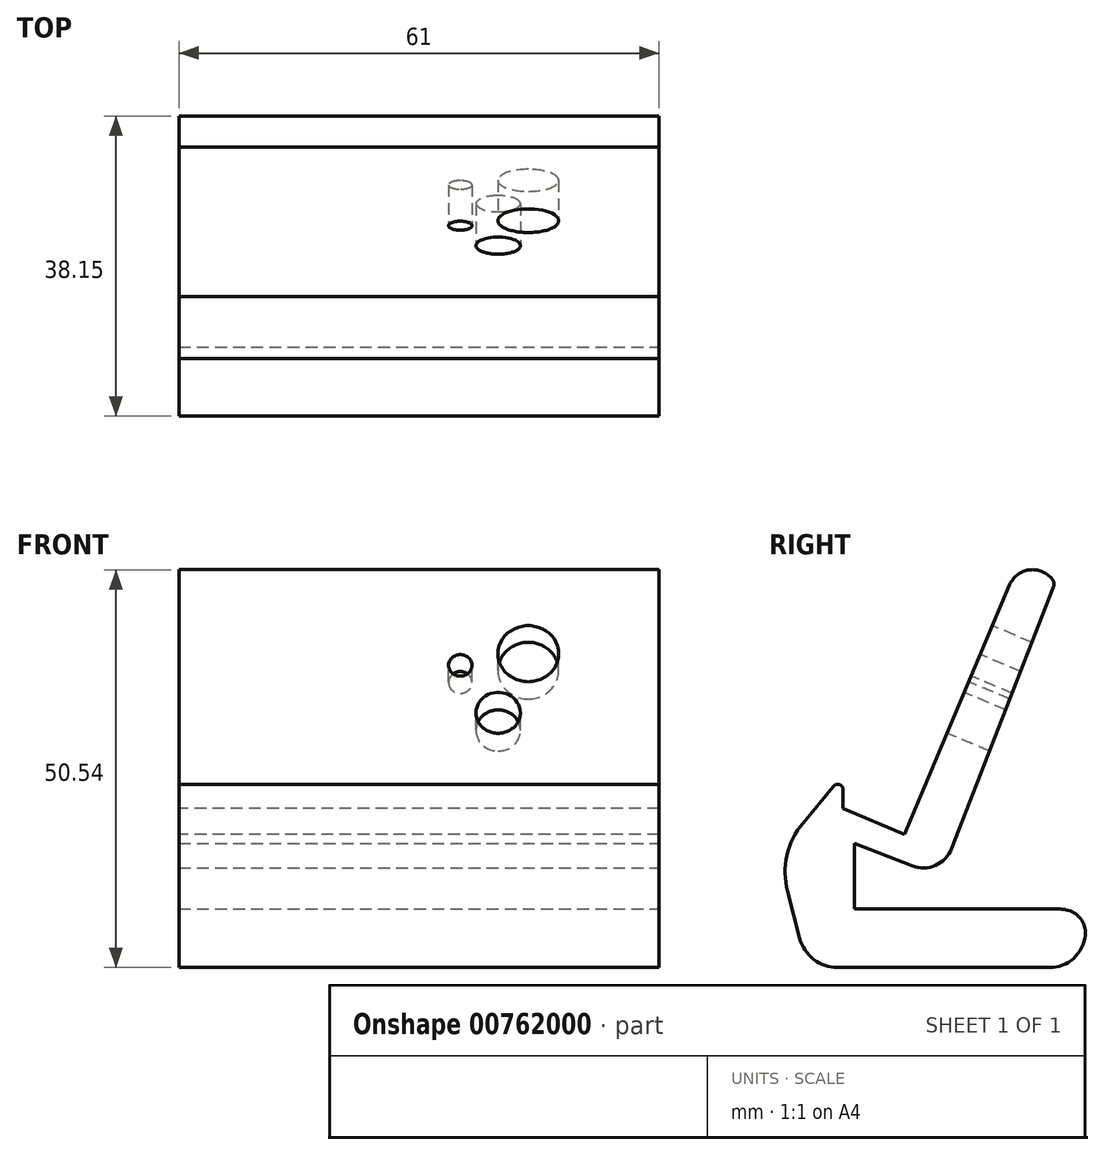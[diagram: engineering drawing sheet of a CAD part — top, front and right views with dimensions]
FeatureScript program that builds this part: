
annotation { "Feature Type Name" : "Feature", "Feature Type Description" : "" }
export const myFeature = defineFeature(function(context is Context, id is Id, definition is map)
    precondition{}
    {
        {
            var Q0;
            Q0=qCreatedBy(makeId("Right.planeOp"),FACE);
            var sketch = newSketch(context, id + "F0", { "sketchPlane" : qUnion([Q0])});
            skLineSegment(sketch, "E0", {"start": v(4.97, 18.95) * mm, "end": v(-10.62, -18.14) * mm});
            skLineSegment(sketch, "E1", {"start": v(-10.62, -18.14) * mm, "end": v(-18.45, -14.85) * mm});
            skLineSegment(sketch, "E2", {"start": v(-18.45, -14.85) * mm, "end": v(-18.45, -10.62) * mm});
            skLineSegment(sketch, "E3", {"start": v(-18.45, -10.62) * mm, "end": v(-26.74, -20.56) * mm});
            skLineSegment(sketch, "E4", {"start": v(-26.74, -20.56) * mm, "end": v(-22.98, -35.08) * mm});
            skLineSegment(sketch, "E5", {"start": v(-22.98, -35.08) * mm, "end": v(18.14, -35.08) * mm});
            skFitSpline(sketch, "E6", {"points": [v(18.14, -35.08) * mm, v(4.97, 18.95) * mm], "startDerivative": vector(-54.43, 31.45) * mm, "endDerivative": vector(-48.38, 56.85) * mm});
            skSolve(sketch);
        }
        {
            var Q0;
            Q0 = qSketchRegion(id + "F0", true);
            extrude(context, id + "F1", {"entities" : qUnion([Q0]), "depth" : 61 * mm, "offsetDistance" : 25 * mm});
        }
        {
            var Q0;
            Q0=makeQuery(id+"F1.opExtrude","SWEPT_EDGE",EDGE,{"disambiguationData":[OSD([sQuery(id+"F0.wireOp",EDGE,"E3"),sQuery(id+"F0.wireOp",EDGE,"E4")])]});
            fillet(context, id + "F2", {"entities" : qUnion([Q0]), "radius" : 9.67 * mm, "tangentPropagation" : true, "allowEdgeOverflow" : false});
        }
        {
            var Q0;
            Q0=makeQuery(id+"F1.opExtrude","SWEPT_EDGE",EDGE,{"disambiguationData":[OSD([sQuery(id+"F0.wireOp",EDGE,"E2"),sQuery(id+"F0.wireOp",EDGE,"E3")])]});
            fillet(context, id + "F3", {"entities" : qUnion([Q0]), "radius" : 0.67 * mm, "tangentPropagation" : true, "allowEdgeOverflow" : false});
        }
        {
            var Q0;
            Q0=makeQuery(id+"F1.opExtrude","SWEPT_EDGE",EDGE,{"disambiguationData":[OSD([sQuery(id+"F0.wireOp",EDGE,"E0"),sQuery(id+"F0.wireOp",EDGE,"E6")])]});
            fillet(context, id + "F4", {"entities" : qUnion([Q0]), "radius" : 3.2 * mm, "tangentPropagation" : true, "allowEdgeOverflow" : false});
        }
        {
            var Q0;
            Q0=makeQuery(id+"F1.opExtrude","SWEPT_EDGE",EDGE,{"disambiguationData":[OSD([sQuery(id+"F0.wireOp",EDGE,"E5"),sQuery(id+"F0.wireOp",EDGE,"E6")])]});
            fillet(context, id + "F5", {"entities" : qUnion([Q0]), "radius" : 4.54 * mm, "tangentPropagation" : true, "allowEdgeOverflow" : false});
        }
        {
            var Q0;
            Q0=makeQuery(id+"F1.opExtrude","SWEPT_EDGE",EDGE,{"disambiguationData":[OSD([sQuery(id+"F0.wireOp",EDGE,"E4"),sQuery(id+"F0.wireOp",EDGE,"E5")])]});
            fillet(context, id + "F6", {"entities" : qUnion([Q0]), "radius" : 5 * mm, "tangentPropagation" : true, "allowEdgeOverflow" : false});
        }
        {
            var Q0;
            Q0=makeQuery(id+"F1.opExtrude","SWEPT_FACE",FACE,{"disambiguationData":[OSD([sQuery(id+"F0.wireOp",EDGE,"E0")])]});
            var sketch = newSketch(context, id + "F7", { "sketchPlane" : qUnion([Q0])});
            skCircle(sketch, "E7", {"center": v(44.4, 4.04) * mm, "radius": 3.87 * mm});
            skCircle(sketch, "E8", {"center": v(35.75, 2.44) * mm, "radius": 1.49 * mm});
            skCircle(sketch, "E9", {"center": v(40.56, -4.1) * mm, "radius": 2.82 * mm});
            skSolve(sketch);
        }
        {
            var Q0;
            Q0 = qSketchRegion(id + "F7", true);
            extrude(context, id + "F8", {"entities" : qUnion([Q0]), "operationType" : NewBodyOperationType.REMOVE, "oppositeDirection" : true, "depth" : 25 * mm, "offsetDistance" : 25 * mm});
        }
        {
            var Q0;
            Q0=makeQuery(id+"F1.opExtrude","CAP_FACE",FACE,{"disambiguationData":[OSD([sQuery(id+"F0.wireOp",EDGE,"E0"),sQuery(id+"F0.wireOp",EDGE,"E1"),sQuery(id+"F0.wireOp",EDGE,"E2"),sQuery(id+"F0.wireOp",EDGE,"E3"),sQuery(id+"F0.wireOp",EDGE,"E4"),sQuery(id+"F0.wireOp",EDGE,"E5"),sQuery(id+"F0.wireOp",EDGE,"E6")])],"isStart":false});
            var sketch = newSketch(context, id + "F9", { "sketchPlane" : qUnion([Q0])});
            skLineSegment(sketch, "E10", {"start": v(8.47, 13.72) * mm, "end": v(-6.05, -23.57) * mm});
            skLineSegment(sketch, "E11", {"start": v(-6.05, -23.57) * mm, "end": v(-17.02, -19.3) * mm});
            skLineSegment(sketch, "E12", {"start": v(-17.02, -19.3) * mm, "end": v(-17.02, -27.65) * mm});
            skLineSegment(sketch, "E13", {"start": v(-17.02, -27.65) * mm, "end": v(21.48, -27.65) * mm});
            skLineSegment(sketch, "E14", {"start": v(8.47, 13.72) * mm, "end": v(17.76, 10.1) * mm});
            skLineSegment(sketch, "E15", {"start": v(17.76, 10.1) * mm, "end": v(21.48, -27.65) * mm});
            skSolve(sketch);
        }
        {
            var Q0;
            Q0 = qSketchRegion(id + "F9", true);
            extrude(context, id + "F10", {"entities" : qUnion([Q0]), "operationType" : NewBodyOperationType.REMOVE, "oppositeDirection" : true, "depth" : 75.5 * mm, "offsetDistance" : 25 * mm});
        }
        {
            var Q0;
            Q0=makeQuery(id+"F10.boolean.opBoolean","COPY",EDGE,{"derivedFrom":makeQuery(id+"F10.opExtrude","SWEPT_EDGE",EDGE,{"disambiguationData":[OSD([sQuery(id+"F9.wireOp",EDGE,"E10"),sQuery(id+"F9.wireOp",EDGE,"E11")])]})});
            fillet(context, id + "F11", {"entities" : qUnion([Q0]), "radius" : 3.86 * mm, "tangentPropagation" : true, "allowEdgeOverflow" : false});
        }
        {
            var Q0;
            Q0=makeQuery(id+"F10.boolean.opBoolean","INTERSECT",EDGE,{"derivedFrom":[makeQuery(id+"F1.opExtrude","SWEPT_FACE",FACE,{"disambiguationData":[OSD([sQuery(id+"F0.wireOp",EDGE,"E6")])]}),makeQuery(id+"F10.opExtrude","SWEPT_FACE",FACE,{"disambiguationData":[OSD([sQuery(id+"F9.wireOp",EDGE,"E13")])]})]});
            fillet(context, id + "F12", {"entities" : qUnion([Q0]), "radius" : 5 * mm, "tangentPropagation" : true, "allowEdgeOverflow" : false});
        }
        {
            var Q0;
            {var subQ0=sQuery(id+"F0.wireOp",EDGE,"E6");Q0=makeQuery(id+"F12.opFillet","BLEND_EDGE",EDGE,{"blendedFrom":[makeQuery(id+"F10.boolean.opBoolean","INTERSECT",EDGE,{"derivedFrom":[makeQuery(id+"F1.opExtrude","SWEPT_FACE",FACE,{"disambiguationData":[OSD([subQ0])]}),makeQuery(id+"F10.opExtrude","SWEPT_FACE",FACE,{"disambiguationData":[OSD([sQuery(id+"F9.wireOp",EDGE,"E13")])]})]}),makeQuery(id+"F5.opFillet","BLEND_FACE",FACE,{"disambiguationData":[OSD([sQuery(id+"F0.wireOp",EDGE,"E5"),subQ0])]})],"blendedInto":[makeQuery(id+"F5.opFillet","BLEND_FACE",FACE,{"disambiguationData":[OSD([sQuery(id+"F0.wireOp",EDGE,"E5"),subQ0])]})]});}
            fillet(context, id + "F13", {"entities" : qUnion([Q0]), "radius" : 3 * mm, "tangentPropagation" : true, "allowEdgeOverflow" : false});
        }
        {
            var Q0;
            {var subQ0=sQuery(id+"F0.wireOp",EDGE,"E6");var subQ1=sQuery(id+"F0.wireOp",EDGE,"E0");Q0=makeQuery(id+"F10.boolean.opBoolean","MERGE",EDGE,{"derivedFrom":[makeQuery(id+"F4.opFillet","BLEND_EDGE",EDGE,{"blendedFrom":[makeQuery(id+"F1.opExtrude","SWEPT_EDGE",EDGE,{"disambiguationData":[OSD([subQ1,subQ0])]}),makeQuery(id+"F1.opExtrude","SWEPT_FACE",FACE,{"disambiguationData":[OSD([subQ0])]})],"blendedInto":[makeQuery(id+"F1.opExtrude","SWEPT_FACE",FACE,{"disambiguationData":[OSD([subQ0])]})]}),makeQuery(id+"F10.opExtrude","SWEPT_EDGE",EDGE,{"disambiguationData":[OSD([subQ1,sQuery(id+"F0.wireOp",EDGE,"E1"),sQuery(id+"F0.wireOp",EDGE,"E2"),sQuery(id+"F0.wireOp",EDGE,"E3"),sQuery(id+"F0.wireOp",EDGE,"E4"),sQuery(id+"F0.wireOp",EDGE,"E5"),subQ0,sQuery(id+"F9.wireOp",EDGE,"E10"),sQuery(id+"F9.wireOp",EDGE,"E14")])]})]});}
            fillet(context, id + "F14", {"entities" : qUnion([Q0]), "radius" : 1 * mm, "tangentPropagation" : true, "allowEdgeOverflow" : false});
        }
    });
